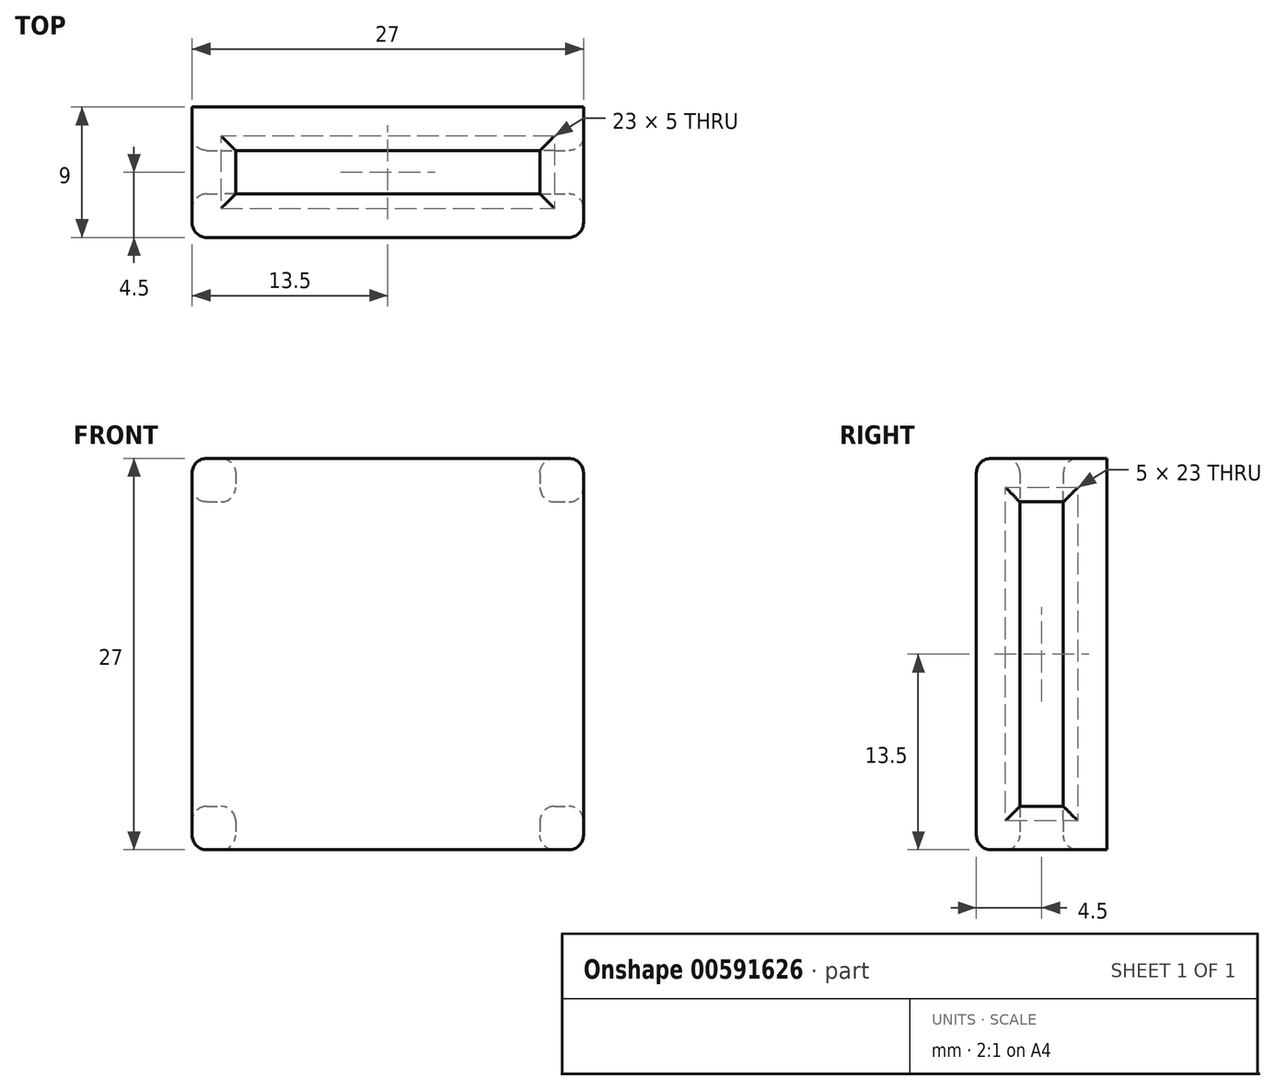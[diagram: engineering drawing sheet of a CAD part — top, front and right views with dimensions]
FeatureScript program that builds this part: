
annotation { "Feature Type Name" : "Feature", "Feature Type Description" : "" }
export const myFeature = defineFeature(function(context is Context, id is Id, definition is map)
    precondition{}
    {
        {
            var Q0;
            Q0=qCreatedBy(makeId("Front.planeOp"),FACE);
            var sketch = newSketch(context, id + "F0", { "sketchPlane" : qUnion([Q0])});
            skLineSegment(sketch, "E0.bottom", {"start": v(-13.5, 13.5) * mm, "end": v(13.5, 13.5) * mm});
            skLineSegment(sketch, "E0.top", {"start": v(-13.5, -13.5) * mm, "end": v(13.5, -13.5) * mm});
            skLineSegment(sketch, "E0.left", {"start": v(-13.5, 13.5) * mm, "end": v(-13.5, -13.5) * mm});
            skLineSegment(sketch, "E0.right", {"start": v(13.5, 13.5) * mm, "end": v(13.5, -13.5) * mm});
            skPoint(sketch, "E0.middle", {"position": v(0, 0) * mm});
            skSolve(sketch);
        }
        {
            var Q0;
            Q0 = qSketchRegion(id + "F0", true);
            extrude(context, id + "F1", {"entities" : qUnion([Q0]), "depth" : 3 * mm, "offsetDistance" : 25 * mm});
        }
        {
            var Q0;
            Q0=makeQuery(id+"F1.opExtrude","CAP_FACE",FACE,{"disambiguationData":[OSD([sQuery(id+"F0.wireOp",EDGE,"E0.bottom"),sQuery(id+"F0.wireOp",EDGE,"E0.top"),sQuery(id+"F0.wireOp",EDGE,"E0.left"),sQuery(id+"F0.wireOp",EDGE,"E0.right")])],"isStart":false});
            var sketch = newSketch(context, id + "F2", { "sketchPlane" : qUnion([Q0])});
            skLineSegment(sketch, "E1.bottom", {"start": v(-13.5, 13.5) * mm, "end": v(-10.5, 13.5) * mm});
            skLineSegment(sketch, "E1.top", {"start": v(-13.5, 10.5) * mm, "end": v(-10.5, 10.5) * mm});
            skLineSegment(sketch, "E1.left", {"start": v(-13.5, 13.5) * mm, "end": v(-13.5, 10.5) * mm});
            skLineSegment(sketch, "E1.right", {"start": v(-10.5, 13.5) * mm, "end": v(-10.5, 10.5) * mm});
            skLineSegment(sketch, "E2.bottom", {"start": v(10.5, 13.5) * mm, "end": v(13.5, 13.5) * mm});
            skLineSegment(sketch, "E2.top", {"start": v(10.5, 10.5) * mm, "end": v(13.5, 10.5) * mm});
            skLineSegment(sketch, "E2.left", {"start": v(10.5, 13.5) * mm, "end": v(10.5, 10.5) * mm});
            skLineSegment(sketch, "E2.right", {"start": v(13.5, 13.5) * mm, "end": v(13.5, 10.5) * mm});
            skLineSegment(sketch, "E3.bottom", {"start": v(10.5, -10.5) * mm, "end": v(13.5, -10.5) * mm});
            skLineSegment(sketch, "E3.top", {"start": v(10.5, -13.5) * mm, "end": v(13.5, -13.5) * mm});
            skLineSegment(sketch, "E3.left", {"start": v(10.5, -10.5) * mm, "end": v(10.5, -13.5) * mm});
            skLineSegment(sketch, "E3.right", {"start": v(13.5, -10.5) * mm, "end": v(13.5, -13.5) * mm});
            skLineSegment(sketch, "E4.bottom", {"start": v(-13.5, -10.5) * mm, "end": v(-10.5, -10.5) * mm});
            skLineSegment(sketch, "E4.top", {"start": v(-13.5, -13.5) * mm, "end": v(-10.5, -13.5) * mm});
            skLineSegment(sketch, "E4.left", {"start": v(-13.5, -10.5) * mm, "end": v(-13.5, -13.5) * mm});
            skLineSegment(sketch, "E4.right", {"start": v(-10.5, -10.5) * mm, "end": v(-10.5, -13.5) * mm});
            skSolve(sketch);
        }
        {
            var Q0;
            Q0 = qSketchRegion(id + "F2", true);
            extrude(context, id + "F3", {"entities" : qUnion([Q0]), "operationType" : NewBodyOperationType.ADD, "depth" : 3 * mm, "offsetDistance" : 25 * mm});
        }
        {
            var Q0;
            Q0=makeQuery(id+"F3.opExtrude","CAP_FACE",FACE,{"disambiguationData":[OSD([sQuery(id+"F2.wireOp",EDGE,"E2.bottom"),sQuery(id+"F2.wireOp",EDGE,"E2.top"),sQuery(id+"F2.wireOp",EDGE,"E2.left"),sQuery(id+"F2.wireOp",EDGE,"E2.right")])],"isStart":false});
            var sketch = newSketch(context, id + "F4", { "sketchPlane" : qUnion([Q0])});
            skLineSegment(sketch, "E5.bottom", {"start": v(13.5, 13.5) * mm, "end": v(-13.5, 13.5) * mm});
            skLineSegment(sketch, "E5.top", {"start": v(13.5, -13.5) * mm, "end": v(-13.5, -13.5) * mm});
            skLineSegment(sketch, "E5.left", {"start": v(13.5, 13.5) * mm, "end": v(13.5, -13.5) * mm});
            skLineSegment(sketch, "E5.right", {"start": v(-13.5, 13.5) * mm, "end": v(-13.5, -13.5) * mm});
            skPoint(sketch, "E5.middle", {"position": v(0, 0) * mm});
            skSolve(sketch);
        }
        {
            var Q0;
            Q0 = qSketchRegion(id + "F4", true);
            extrude(context, id + "F5", {"entities" : qUnion([Q0]), "operationType" : NewBodyOperationType.ADD, "depth" : 3 * mm, "offsetDistance" : 25 * mm});
        }
        {
            var Q0;
            Q0=makeQuery(id+"F5.opExtrude","CAP_EDGE",EDGE,{"disambiguationData":[OSD([sQuery(id+"F4.wireOp",EDGE,"E5.right")])],"isStart":false});
            var Q1;
            Q1=makeQuery(id+"F5.opExtrude","CAP_EDGE",EDGE,{"disambiguationData":[OSD([sQuery(id+"F4.wireOp",EDGE,"E5.bottom")])],"isStart":false});
            var Q2;
            Q2=makeQuery(id+"F5.opExtrude","CAP_EDGE",EDGE,{"disambiguationData":[OSD([sQuery(id+"F4.wireOp",EDGE,"E5.left")])],"isStart":false});
            var Q3;
            Q3=makeQuery(id+"F5.opExtrude","CAP_EDGE",EDGE,{"disambiguationData":[OSD([sQuery(id+"F4.wireOp",EDGE,"E5.top")])],"isStart":false});
            var Q4;
            Q4=makeQuery(id+"F1.opExtrude","CAP_EDGE",EDGE,{"disambiguationData":[OSD([sQuery(id+"F0.wireOp",EDGE,"E0.left")])],"isStart":false});
            var Q5;
            Q5=makeQuery(id+"F5.opExtrude","CAP_EDGE",EDGE,{"disambiguationData":[OSD([sQuery(id+"F4.wireOp",EDGE,"E5.right")])],"isStart":true});
            var Q6;
            Q6=makeQuery(id+"F3.opExtrude","SWEPT_EDGE",EDGE,{"disambiguationData":[OSD([sQuery(id+"F0.wireOp",EDGE,"E0.left"),sQuery(id+"F2.wireOp",EDGE,"E1.top"),sQuery(id+"F2.wireOp",EDGE,"E1.left")])]});
            var Q7;
            Q7=makeQuery(id+"F3.opExtrude","SWEPT_EDGE",EDGE,{"disambiguationData":[OSD([sQuery(id+"F0.wireOp",EDGE,"E0.left"),sQuery(id+"F2.wireOp",EDGE,"E4.bottom"),sQuery(id+"F2.wireOp",EDGE,"E4.left")])]});
            var Q8;
            Q8=makeQuery(id+"F5.opExtrude","CAP_EDGE",EDGE,{"disambiguationData":[OSD([sQuery(id+"F4.wireOp",EDGE,"E5.top")])],"isStart":true});
            var Q9;
            Q9=makeQuery(id+"F3.opExtrude","SWEPT_EDGE",EDGE,{"disambiguationData":[OSD([sQuery(id+"F0.wireOp",EDGE,"E0.top"),sQuery(id+"F2.wireOp",EDGE,"E4.top"),sQuery(id+"F2.wireOp",EDGE,"E4.right")])]});
            var Q10;
            Q10=makeQuery(id+"F1.opExtrude","CAP_EDGE",EDGE,{"disambiguationData":[OSD([sQuery(id+"F0.wireOp",EDGE,"E0.top")])],"isStart":false});
            var Q11;
            Q11=makeQuery(id+"F3.opExtrude","SWEPT_EDGE",EDGE,{"disambiguationData":[OSD([sQuery(id+"F0.wireOp",EDGE,"E0.top"),sQuery(id+"F2.wireOp",EDGE,"E3.top"),sQuery(id+"F2.wireOp",EDGE,"E3.left")])]});
            var Q12;
            Q12=makeQuery(id+"F3.opExtrude","SWEPT_EDGE",EDGE,{"disambiguationData":[OSD([sQuery(id+"F0.wireOp",EDGE,"E0.right"),sQuery(id+"F2.wireOp",EDGE,"E3.bottom"),sQuery(id+"F2.wireOp",EDGE,"E3.right")])]});
            var Q13;
            Q13=makeQuery(id+"F5.opExtrude","CAP_EDGE",EDGE,{"disambiguationData":[OSD([sQuery(id+"F4.wireOp",EDGE,"E5.left")])],"isStart":true});
            var Q14;
            Q14=makeQuery(id+"F3.opExtrude","SWEPT_EDGE",EDGE,{"disambiguationData":[OSD([sQuery(id+"F0.wireOp",EDGE,"E0.right"),sQuery(id+"F2.wireOp",EDGE,"E2.top"),sQuery(id+"F2.wireOp",EDGE,"E2.right")])]});
            var Q15;
            Q15=makeQuery(id+"F1.opExtrude","CAP_EDGE",EDGE,{"disambiguationData":[OSD([sQuery(id+"F0.wireOp",EDGE,"E0.right")])],"isStart":false});
            var Q16;
            Q16=makeQuery(id+"F3.opExtrude","SWEPT_EDGE",EDGE,{"disambiguationData":[OSD([sQuery(id+"F0.wireOp",EDGE,"E0.bottom"),sQuery(id+"F2.wireOp",EDGE,"E2.bottom"),sQuery(id+"F2.wireOp",EDGE,"E2.left")])]});
            var Q17;
            Q17=makeQuery(id+"F5.opExtrude","CAP_EDGE",EDGE,{"disambiguationData":[OSD([sQuery(id+"F4.wireOp",EDGE,"E5.bottom")])],"isStart":true});
            var Q18;
            Q18=makeQuery(id+"F3.opExtrude","SWEPT_EDGE",EDGE,{"disambiguationData":[OSD([sQuery(id+"F0.wireOp",EDGE,"E0.bottom"),sQuery(id+"F2.wireOp",EDGE,"E1.bottom"),sQuery(id+"F2.wireOp",EDGE,"E1.right")])]});
            var Q19;
            Q19=makeQuery(id+"F1.opExtrude","CAP_EDGE",EDGE,{"disambiguationData":[OSD([sQuery(id+"F0.wireOp",EDGE,"E0.bottom")])],"isStart":false});
            var Q20;
            Q20=makeQuery(id+"F3.opExtrude","SWEPT_EDGE",EDGE,{"disambiguationData":[OSD([sQuery(id+"F2.wireOp",EDGE,"E2.top"),sQuery(id+"F2.wireOp",EDGE,"E2.left")])]});
            var Q21;
            Q21=makeQuery(id+"F3.opExtrude","SWEPT_EDGE",EDGE,{"disambiguationData":[OSD([sQuery(id+"F2.wireOp",EDGE,"E3.bottom"),sQuery(id+"F2.wireOp",EDGE,"E3.left")])]});
            var Q22;
            Q22=makeQuery(id+"F3.opExtrude","SWEPT_EDGE",EDGE,{"disambiguationData":[OSD([sQuery(id+"F2.wireOp",EDGE,"E4.bottom"),sQuery(id+"F2.wireOp",EDGE,"E4.right")])]});
            var Q23;
            Q23=makeQuery(id+"F3.opExtrude","SWEPT_EDGE",EDGE,{"disambiguationData":[OSD([sQuery(id+"F2.wireOp",EDGE,"E1.top"),sQuery(id+"F2.wireOp",EDGE,"E1.right")])]});
            var Q24;
            Q24=makeQuery(id+"F5.boolean.opBoolean","MERGE",EDGE,{"derivedFrom":[makeQuery(id+"F3.boolean.opBoolean","MERGE",EDGE,{"derivedFrom":[makeQuery(id+"F1.opExtrude","SWEPT_EDGE",EDGE,{"disambiguationData":[OSD([sQuery(id+"F0.wireOp",EDGE,"E0.bottom"),sQuery(id+"F0.wireOp",EDGE,"E0.left")])]}),makeQuery(id+"F3.opExtrude","SWEPT_EDGE",EDGE,{"disambiguationData":[OSD([sQuery(id+"F2.wireOp",EDGE,"E1.bottom"),sQuery(id+"F2.wireOp",EDGE,"E1.left")])]})]}),makeQuery(id+"F5.opExtrude","SWEPT_EDGE",EDGE,{"disambiguationData":[OSD([sQuery(id+"F4.wireOp",EDGE,"E5.bottom"),sQuery(id+"F4.wireOp",EDGE,"E5.right")])]})]});
            var Q25;
            Q25=makeQuery(id+"F5.boolean.opBoolean","MERGE",EDGE,{"derivedFrom":[makeQuery(id+"F3.boolean.opBoolean","MERGE",EDGE,{"derivedFrom":[makeQuery(id+"F1.opExtrude","SWEPT_EDGE",EDGE,{"disambiguationData":[OSD([sQuery(id+"F0.wireOp",EDGE,"E0.bottom"),sQuery(id+"F0.wireOp",EDGE,"E0.right")])]}),makeQuery(id+"F3.opExtrude","SWEPT_EDGE",EDGE,{"disambiguationData":[OSD([sQuery(id+"F2.wireOp",EDGE,"E2.bottom"),sQuery(id+"F2.wireOp",EDGE,"E2.right")])]})]}),makeQuery(id+"F5.opExtrude","SWEPT_EDGE",EDGE,{"disambiguationData":[OSD([sQuery(id+"F4.wireOp",EDGE,"E5.bottom"),sQuery(id+"F4.wireOp",EDGE,"E5.left")])]})]});
            var Q26;
            Q26=makeQuery(id+"F5.boolean.opBoolean","MERGE",EDGE,{"derivedFrom":[makeQuery(id+"F3.boolean.opBoolean","MERGE",EDGE,{"derivedFrom":[makeQuery(id+"F1.opExtrude","SWEPT_EDGE",EDGE,{"disambiguationData":[OSD([sQuery(id+"F0.wireOp",EDGE,"E0.top"),sQuery(id+"F0.wireOp",EDGE,"E0.right")])]}),makeQuery(id+"F3.opExtrude","SWEPT_EDGE",EDGE,{"disambiguationData":[OSD([sQuery(id+"F2.wireOp",EDGE,"E3.top"),sQuery(id+"F2.wireOp",EDGE,"E3.right")])]})]}),makeQuery(id+"F5.opExtrude","SWEPT_EDGE",EDGE,{"disambiguationData":[OSD([sQuery(id+"F4.wireOp",EDGE,"E5.top"),sQuery(id+"F4.wireOp",EDGE,"E5.left")])]})]});
            var Q27;
            Q27=makeQuery(id+"F5.boolean.opBoolean","MERGE",EDGE,{"derivedFrom":[makeQuery(id+"F3.boolean.opBoolean","MERGE",EDGE,{"derivedFrom":[makeQuery(id+"F1.opExtrude","SWEPT_EDGE",EDGE,{"disambiguationData":[OSD([sQuery(id+"F0.wireOp",EDGE,"E0.top"),sQuery(id+"F0.wireOp",EDGE,"E0.left")])]}),makeQuery(id+"F3.opExtrude","SWEPT_EDGE",EDGE,{"disambiguationData":[OSD([sQuery(id+"F2.wireOp",EDGE,"E4.top"),sQuery(id+"F2.wireOp",EDGE,"E4.left")])]})]}),makeQuery(id+"F5.opExtrude","SWEPT_EDGE",EDGE,{"disambiguationData":[OSD([sQuery(id+"F4.wireOp",EDGE,"E5.top"),sQuery(id+"F4.wireOp",EDGE,"E5.right")])]})]});
            fillet(context, id + "F6", {"entities" : qUnion([Q0, Q1, Q2, Q3, Q4, Q5, Q6, Q7, Q8, Q9, Q10, Q11, Q12, Q13, Q14, Q15, Q16, Q17, Q18, Q19, Q20, Q21, Q22, Q23, Q24, Q25, Q26, Q27]), "radius" : 1 * mm, "tangentPropagation" : true, "allowEdgeOverflow" : false});
        }
    });
